# Revit family: FEHK 2 WIDE (HORIZONTAL THROW)
name_source: partatom
category: Cable Tray Fittings
units: mm (PartAtom-declared; Revit-internal decimal feet)

## family parameters
Always vertical = Yes
Cut with Voids When Loaded = No
Part Type = Channel Elbow
Round Connector Dimension = Use Diameter
Shared = No
Work Plane-Based = No

## types (6) — shared parameters
Description = 2 WIDE FLUID COOLER WITH K FAN MOTOR
Fan001 = Yes
Fan002 = Yes
HEIGHT = 90.5 "
Manufacturer = Krack Corporation
Overall Width = 36 "
Revit Family Dates = 09/04/2023HM
Top support visibility = Yes
Type Comments = KR Series 2-Fan Condenser
URL = www.krack.com
Width = 28 "

## per-type parameters (varying)
| type | Copper Pipes | F3 | F4 | F5 | F6 | F7 | Fan003 | Fan004 | Fan005 | Fan006 | Fan007 | Length | Model | Top Support |
| FEHK 2X4 | <By Category> | Yes | Yes | No | No | No | Yes | Yes | No | No | No | 220 " | FEHK 2 X 4 | Top Support top : F4 |
| FEHK 2X5 | <By Category> | Yes | Yes | Yes | No | No | Yes | Yes | Yes | No | No | 274 " | FEHK 2 X5 | Top Support top : F5 |
| FEHK 2X3 | Copper | Yes | No | No | No | No | Yes | No | No | No | No | 166 " | FEHK 2X3 | Top Support top : F3 |
| FEHK 2X2 | Copper | No | No | No | No | No | No | No | No | No | No | 112 " | FEHK 2 X2 | Top Support top : F2 |
| FEHK 2X6 | Copper | Yes | Yes | Yes | Yes | No | Yes | Yes | Yes | Yes | No | 328 " | FEHK 2X6 | Top Support top : F6 |
| FEHK 2X7 | Copper | Yes | Yes | Yes | Yes | Yes | Yes | Yes | Yes | Yes | Yes | 382 " | FEHK 2 X7 | Top Support top : F7 |

## geometry (parser evidence)
native form markers: Sweep x17
no freeform markers — native parametric forms only
